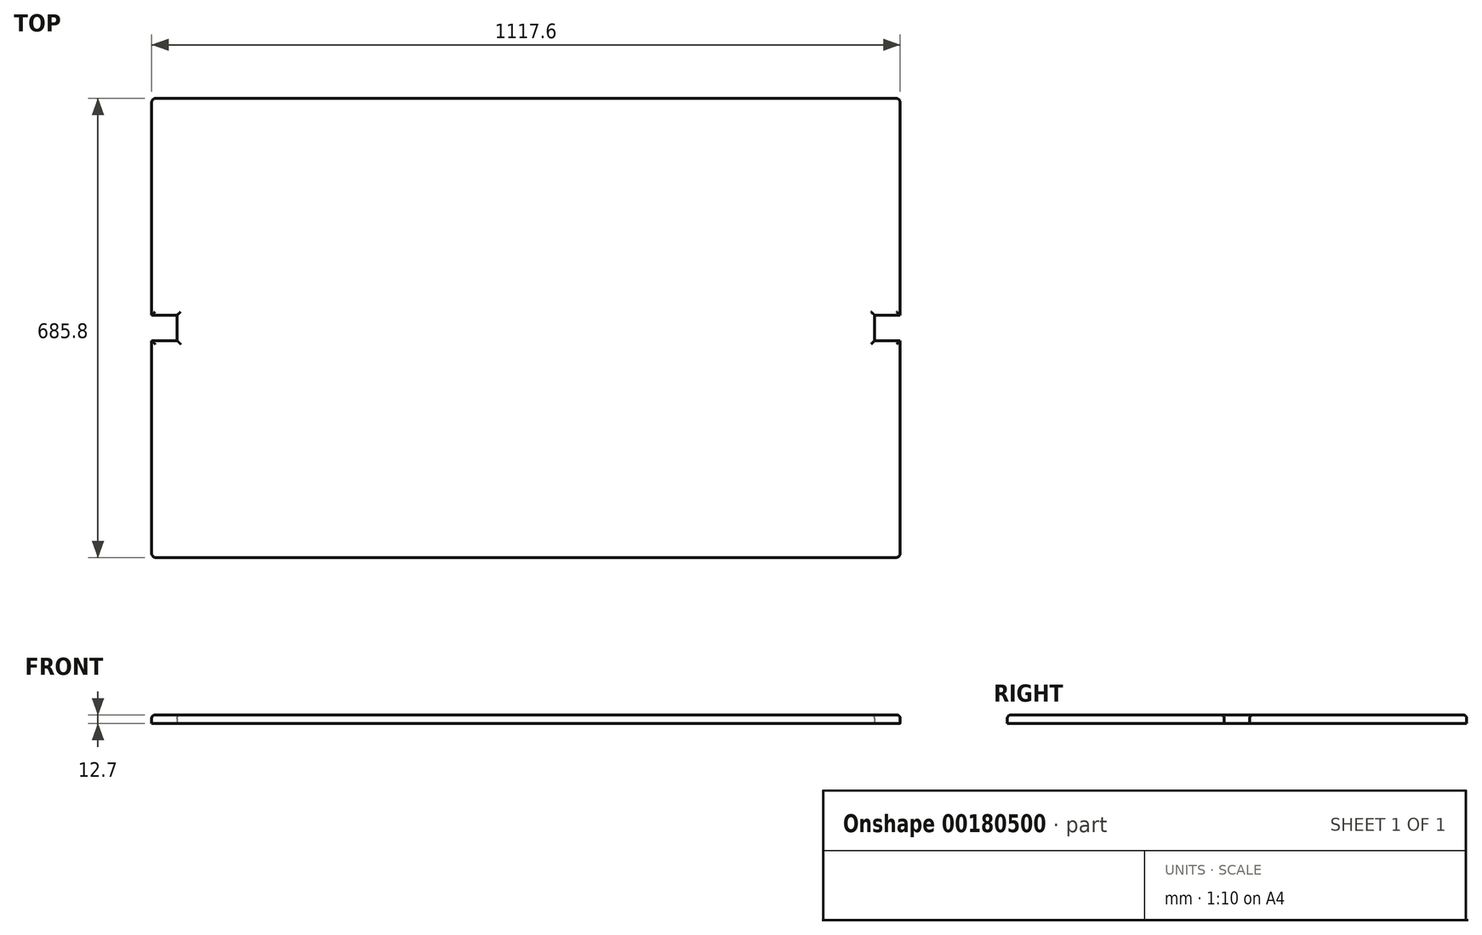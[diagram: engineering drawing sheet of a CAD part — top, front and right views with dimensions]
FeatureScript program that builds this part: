
annotation { "Feature Type Name" : "Feature", "Feature Type Description" : "" }
export const myFeature = defineFeature(function(context is Context, id is Id, definition is map)
    precondition{}
    {
        {
            var Q0;
            Q0=qCreatedBy(makeId("Top.planeOp"),FACE);
            var sketch = newSketch(context, id + "F0", { "sketchPlane" : qUnion([Q0])});
            skLineSegment(sketch, "E0.bottom", {"start": v(552.45, -342.9) * mm, "end": v(-552.45, -342.9) * mm});
            skLineSegment(sketch, "E0.top", {"start": v(552.45, 342.9) * mm, "end": v(-552.45, 342.9) * mm});
            skLineSegment(sketch, "E0.left", {"start": v(558.8, -336.55) * mm, "end": v(558.8, -19.05) * mm});
            skLineSegment(sketch, "E0.right", {"start": v(-558.8, -336.55) * mm, "end": v(-558.8, -19.05) * mm});
            skPoint(sketch, "E0.middle", {"position": v(0, 0) * mm});
            skPoint(sketch, "E1.visualSharp", {"position": v(-558.8, 342.9) * mm});
            skArc(sketch, "E1.filletArc", {"start": v(-552.45, 342.9) * mm, "mid": v(-556.94, 341.04) * mm, "end": v(-558.8, 336.55) * mm});
            skPoint(sketch, "E2.visualSharp", {"position": v(-558.8, -342.9) * mm});
            skArc(sketch, "E2.filletArc", {"start": v(-558.8, -336.55) * mm, "mid": v(-556.94, -341.04) * mm, "end": v(-552.45, -342.9) * mm});
            skPoint(sketch, "E3.visualSharp", {"position": v(558.8, -342.9) * mm});
            skArc(sketch, "E3.filletArc", {"start": v(552.45, -342.9) * mm, "mid": v(556.94, -341.04) * mm, "end": v(558.8, -336.55) * mm});
            skPoint(sketch, "E4.visualSharp", {"position": v(558.8, 342.9) * mm});
            skArc(sketch, "E4.filletArc", {"start": v(558.8, 336.55) * mm, "mid": v(556.94, 341.04) * mm, "end": v(552.45, 342.9) * mm});
            skLineSegment(sketch, "E5.bottom", {"start": v(-520.7, -19.05) * mm, "end": v(-558.8, -19.05) * mm});
            skLineSegment(sketch, "E5.top", {"start": v(-520.7, 19.05) * mm, "end": v(-558.8, 19.05) * mm});
            skLineSegment(sketch, "E5.left", {"start": v(-520.7, -19.05) * mm, "end": v(-520.7, 19.05) * mm});
            skLineSegment(sketch, "E6.trimOffspring", {"start": v(-558.8, 19.05) * mm, "end": v(-558.8, 336.55) * mm});
            skLineSegment(sketch, "E7", {"start": v(0, 0) * mm, "end": v(0, 342.9) * mm, "construction": true});
            skLineSegment(sketch, "E8.MirrorCS", {"start": v(520.7, 19.05) * mm, "end": v(558.8, 19.05) * mm});
            skLineSegment(sketch, "E9.MirrorCS", {"start": v(520.7, -19.05) * mm, "end": v(520.7, 19.05) * mm});
            skLineSegment(sketch, "E10.MirrorCS", {"start": v(520.7, -19.05) * mm, "end": v(558.8, -19.05) * mm});
            skLineSegment(sketch, "E11.trimOffspring", {"start": v(558.8, 19.05) * mm, "end": v(558.8, 336.55) * mm});
            skSolve(sketch);
        }
        {
            var Q0;
            Q0=qSketchRegion(id+"F0",true);
            extrude(context, id + "F1", {"entities" : qUnion([Q0]), "depth" : 12.7 * mm});
        }
        {
            var Q0;
            Q0=makeQuery(id+"F1.opExtrude","CAP_FACE",FACE,{"disambiguationData":[OSD([sQuery(id+"F0.wireOp",EDGE,"E0.bottom"),sQuery(id+"F0.wireOp",EDGE,"E0.top"),sQuery(id+"F0.wireOp",EDGE,"E0.left"),sQuery(id+"F0.wireOp",EDGE,"E0.right"),sQuery(id+"F0.wireOp",EDGE,"E1.filletArc"),sQuery(id+"F0.wireOp",EDGE,"E2.filletArc"),sQuery(id+"F0.wireOp",EDGE,"E3.filletArc"),sQuery(id+"F0.wireOp",EDGE,"E4.filletArc")])],"isStart":false});
            fillet(context, id + "F2", {"entities" : qUnion([Q0]), "radius" : 5.08 * mm, "tangentPropagation" : true, "allowEdgeOverflow" : false});
        }
    });
